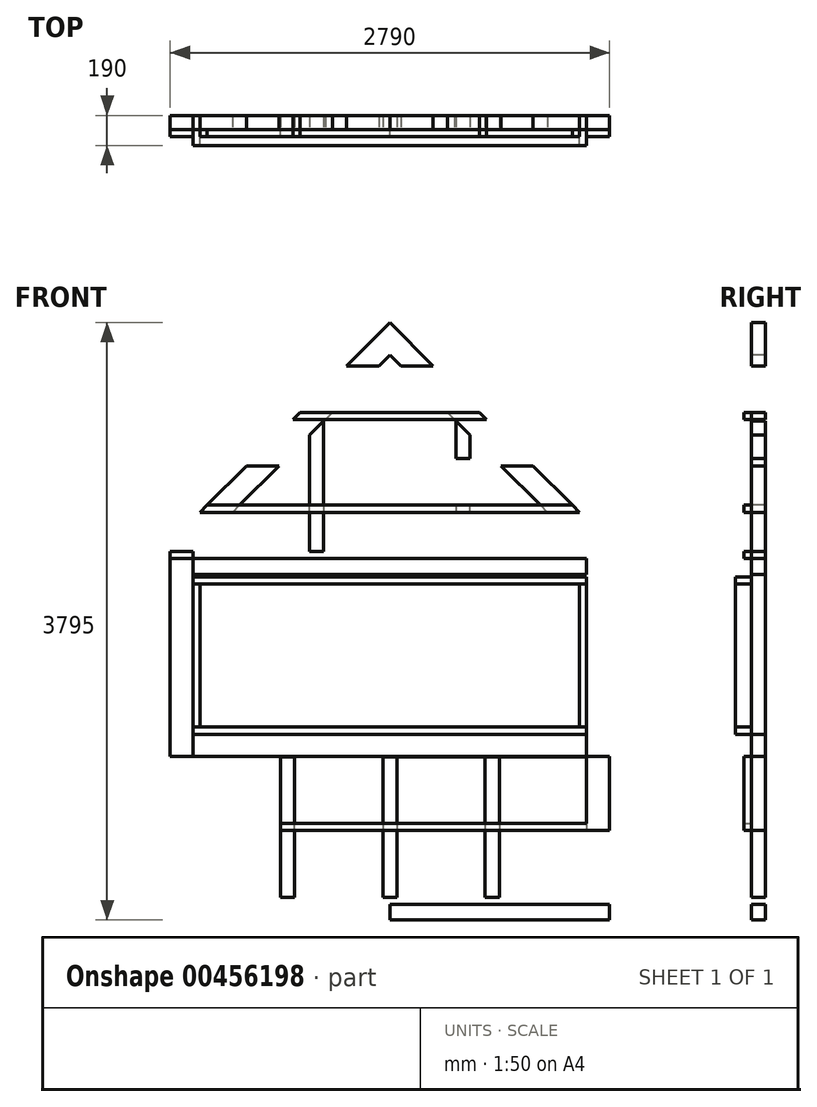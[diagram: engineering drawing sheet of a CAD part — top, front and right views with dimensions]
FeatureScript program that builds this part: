
annotation { "Feature Type Name" : "Feature", "Feature Type Description" : "" }
export const myFeature = defineFeature(function(context is Context, id is Id, definition is map)
    precondition{}
    {
        {
            var Q0;
            Q0=qCreatedBy(makeId("Front.planeOp"),FACE);
            var sketch = newSketch(context, id + "F0", { "sketchPlane" : qUnion([Q0])});
            skLineSegment(sketch, "E0.top", {"start": v(-920.12, -904.5) * mm, "end": v(-3710.12, -904.5) * mm});
            skLineSegment(sketch, "E0.left", {"start": v(-920.12, 1495.5) * mm, "end": v(-920.12, -904.5) * mm});
            skLineSegment(sketch, "E0.right", {"start": v(-3710.12, 1495.5) * mm, "end": v(-3710.12, -904.5) * mm});
            skLineSegment(sketch, "E1", {"start": v(-3710.12, 1495.5) * mm, "end": v(-2315.12, 2890.5) * mm});
            skLineSegment(sketch, "E2", {"start": v(-2315.12, 2890.5) * mm, "end": v(-920.12, 1495.5) * mm});
            skLineSegment(sketch, "E3.0", {"start": v(-2315.12, 2685.45) * mm, "end": v(-1065.12, 1435.45) * mm});
            skLineSegment(sketch, "E3.1", {"start": v(-3565.12, 1435.45) * mm, "end": v(-2315.12, 2685.45) * mm});
            skLineSegment(sketch, "E3.2", {"start": v(-1065.12, 1435.45) * mm, "end": v(-1065.12, -759.5) * mm});
            skLineSegment(sketch, "E3.3", {"start": v(-1065.12, -759.5) * mm, "end": v(-3565.12, -759.5) * mm});
            skLineSegment(sketch, "E3.4", {"start": v(-3565.12, 1435.45) * mm, "end": v(-3565.12, -759.5) * mm});
            skLineSegment(sketch, "E4.0", {"start": v(-2315.12, 2954.15) * mm, "end": v(-875.12, 1514.15) * mm});
            skLineSegment(sketch, "E4.1", {"start": v(-3755.12, 1514.15) * mm, "end": v(-2315.12, 2954.15) * mm});
            skLineSegment(sketch, "E4.2", {"start": v(-875.12, 1514.15) * mm, "end": v(-875.12, -949.5) * mm});
            skLineSegment(sketch, "E4.3", {"start": v(-875.12, -949.5) * mm, "end": v(-3755.12, -949.5) * mm});
            skLineSegment(sketch, "E4.4", {"start": v(-3755.12, 1514.15) * mm, "end": v(-3755.12, -949.5) * mm});
            skLineSegment(sketch, "E5.bottom", {"start": v(-3565.12, -759.5) * mm, "end": v(-2655.12, -759.5) * mm});
            skLineSegment(sketch, "E5.left", {"start": v(-3565.12, -759.5) * mm, "end": v(-3565.12, 1275.5) * mm});
            skLineSegment(sketch, "E6.bottom", {"start": v(-3565.12, 1435.45) * mm, "end": v(-1065.12, 1435.45) * mm});
            skLineSegment(sketch, "E6.top", {"start": v(-3565.12, 1290.45) * mm, "end": v(-1065.12, 1290.45) * mm});
            skLineSegment(sketch, "E6.left", {"start": v(-3565.12, 1435.45) * mm, "end": v(-3565.12, 1290.45) * mm});
            skLineSegment(sketch, "E6.right", {"start": v(-1065.12, 1435.45) * mm, "end": v(-1065.12, 1290.45) * mm});
            skLineSegment(sketch, "E7.left", {"start": v(-1065.12, 1275.5) * mm, "end": v(-1065.12, 275.5) * mm});
            skLineSegment(sketch, "E8.bottom", {"start": v(-3565.12, 1275.5) * mm, "end": v(-1065.12, 1275.5) * mm});
            skLineSegment(sketch, "E8.top", {"start": v(-3565.12, 275.5) * mm, "end": v(-1065.12, 275.5) * mm});
            skLineSegment(sketch, "E8.left", {"start": v(-3565.12, 1275.5) * mm, "end": v(-3565.12, 275.5) * mm});
            skLineSegment(sketch, "E9", {"start": v(-3565.12, 320.5) * mm, "end": v(-1065.12, 320.5) * mm});
            skLineSegment(sketch, "E10", {"start": v(-3565.12, 1230.5) * mm, "end": v(-1065.12, 1230.5) * mm});
            skLineSegment(sketch, "E11", {"start": v(-3520.12, 1230.5) * mm, "end": v(-3520.12, 320.5) * mm});
            skLineSegment(sketch, "E12", {"start": v(-1110.12, 1230.5) * mm, "end": v(-1110.12, 320.5) * mm});
            skLineSegment(sketch, "E13", {"start": v(-3710.12, -904.5) * mm, "end": v(-3755.12, -904.5) * mm});
            skLineSegment(sketch, "E14", {"start": v(-3455.12, -904.5) * mm, "end": v(-3555.12, -904.5) * mm});
            skLineSegment(sketch, "E15", {"start": v(-3255.12, -904.5) * mm, "end": v(-3455.12, -904.5) * mm});
            skLineSegment(sketch, "E16", {"start": v(-2315.12, 2890.5) * mm, "end": v(-2315.12, 2685.45) * mm, "construction": true});
            skLineSegment(sketch, "E17", {"start": v(-2315.12, 320.5) * mm, "end": v(-2315.12, -904.5) * mm});
            skLineSegment(sketch, "E18.bottom", {"start": v(-2315.12, 275.5) * mm, "end": v(-3565.12, 275.5) * mm});
            skLineSegment(sketch, "E18.left", {"start": v(-2315.12, 275.5) * mm, "end": v(-2315.12, 130.5) * mm});
            skLineSegment(sketch, "E18.right", {"start": v(-3565.12, 275.5) * mm, "end": v(-3565.12, 130.5) * mm});
            skLineSegment(sketch, "E19", {"start": v(-2315.12, -759.5) * mm, "end": v(-2315.12, -904.5) * mm});
            skLineSegment(sketch, "E20", {"start": v(-3565.12, 130.5) * mm, "end": v(-1065.12, 130.5) * mm});
            skLineSegment(sketch, "E21.bottom", {"start": v(-3710.12, 130.5) * mm, "end": v(-920.12, 130.5) * mm});
            skLineSegment(sketch, "E21.left", {"start": v(-3710.12, 130.5) * mm, "end": v(-3710.12, 181) * mm});
            skLineSegment(sketch, "E21.right", {"start": v(-920.12, 130.5) * mm, "end": v(-920.12, 181) * mm});
            skLineSegment(sketch, "E22.left", {"start": v(-3710.12, -305.95) * mm, "end": v(-3710.12, -350.95) * mm});
            skLineSegment(sketch, "E22.right", {"start": v(-920.12, -305.95) * mm, "end": v(-920.12, -350.95) * mm});
            skLineSegment(sketch, "E23.right", {"start": v(-920.12, -833.92) * mm, "end": v(-920.12, -788.92) * mm});
            skLineSegment(sketch, "E24.left", {"start": v(-3710.12, 1443.91) * mm, "end": v(-3710.12, 1398.91) * mm});
            skLineSegment(sketch, "E24.right", {"start": v(-920.12, 1443.91) * mm, "end": v(-920.12, 1398.91) * mm});
            skLineSegment(sketch, "E25.left", {"start": v(-3565.12, 1640.5) * mm, "end": v(-3565.12, 1585.75) * mm});
            skLineSegment(sketch, "E25.right", {"start": v(-1081.29, 1640.5) * mm, "end": v(-1081.29, 1585.75) * mm});
            skLineSegment(sketch, "E26.bottom", {"start": v(-3010.12, -759.5) * mm, "end": v(-2920.12, -759.5) * mm});
            skLineSegment(sketch, "E26.top", {"start": v(-3010.12, 130.5) * mm, "end": v(-2920.12, 130.5) * mm});
            skLineSegment(sketch, "E26.left", {"start": v(-3010.12, -759.5) * mm, "end": v(-3010.12, 130.5) * mm});
            skLineSegment(sketch, "E26.right", {"start": v(-2920.12, -759.5) * mm, "end": v(-2920.12, 130.5) * mm});
            skLineSegment(sketch, "E27.bottom", {"start": v(-1710.12, 130.5) * mm, "end": v(-1620.12, 130.5) * mm});
            skLineSegment(sketch, "E27.top", {"start": v(-1710.12, -759.5) * mm, "end": v(-1620.12, -759.5) * mm});
            skLineSegment(sketch, "E27.left", {"start": v(-1710.12, 130.5) * mm, "end": v(-1710.12, -759.5) * mm});
            skLineSegment(sketch, "E27.right", {"start": v(-1620.12, 130.5) * mm, "end": v(-1620.12, -759.5) * mm});
            skLineSegment(sketch, "E28", {"start": v(-2360.12, 130.5) * mm, "end": v(-2360.12, -759.5) * mm});
            skLineSegment(sketch, "E29.MirrorCS", {"start": v(-2270.12, 130.5) * mm, "end": v(-2270.12, -759.5) * mm});
            skLineSegment(sketch, "E30", {"start": v(-2825.12, 1435.45) * mm, "end": v(-2825.12, 2175.45) * mm});
            skLineSegment(sketch, "E31", {"start": v(-2735.12, 2265.45) * mm, "end": v(-2735.12, 1435.45) * mm});
            skLineSegment(sketch, "E32", {"start": v(-2315.12, 2685.45) * mm, "end": v(-2315.12, 130.5) * mm, "construction": true});
            skPoint(sketch, "E33", {"position": v(-2360.12, 1435.45) * mm});
            skLineSegment(sketch, "E34.MirrorCS", {"start": v(-1895.12, 2265.45) * mm, "end": v(-1895.12, 1435.45) * mm});
            skLineSegment(sketch, "E35.MirrorCS", {"start": v(-1805.12, 1435.45) * mm, "end": v(-1805.12, 2175.45) * mm});
            skLineSegment(sketch, "E36", {"start": v(-2735.12, 2265.45) * mm, "end": v(-1895.12, 2265.45) * mm});
            skLineSegment(sketch, "E37", {"start": v(-2735.12, 2175.45) * mm, "end": v(-1895.12, 2175.45) * mm});
            skLineSegment(sketch, "E38.bottom", {"start": v(-3710.12, -759.5) * mm, "end": v(-875.12, -759.5) * mm});
            skLineSegment(sketch, "E38.top", {"start": v(-3710.12, -804.5) * mm, "end": v(-875.12, -804.5) * mm});
            skLineSegment(sketch, "E38.left", {"start": v(-3710.12, -759.5) * mm, "end": v(-3710.12, -804.5) * mm});
            skLineSegment(sketch, "E38.right", {"start": v(-875.12, -759.5) * mm, "end": v(-875.12, -804.5) * mm});
            skLineSegment(sketch, "E39.bottom", {"start": v(-3710.12, -289.5) * mm, "end": v(-920.12, -289.5) * mm});
            skLineSegment(sketch, "E39.top", {"start": v(-3710.12, -334.5) * mm, "end": v(-920.12, -334.5) * mm});
            skLineSegment(sketch, "E39.left", {"start": v(-3710.12, -289.5) * mm, "end": v(-3710.12, -334.5) * mm});
            skLineSegment(sketch, "E39.right", {"start": v(-920.12, -289.5) * mm, "end": v(-920.12, -334.5) * mm});
            skLineSegment(sketch, "E40.bottom", {"start": v(-3710.12, 135.5) * mm, "end": v(-920.12, 135.5) * mm});
            skLineSegment(sketch, "E40.top", {"start": v(-3710.12, 90.5) * mm, "end": v(-920.12, 90.5) * mm});
            skLineSegment(sketch, "E40.left", {"start": v(-3710.12, 135.5) * mm, "end": v(-3710.12, 90.5) * mm});
            skLineSegment(sketch, "E40.right", {"start": v(-920.12, 135.5) * mm, "end": v(-920.12, 90.5) * mm});
            skLineSegment(sketch, "E41.bottom", {"start": v(-3710.12, 1435.45) * mm, "end": v(-920.12, 1435.45) * mm});
            skLineSegment(sketch, "E41.top", {"start": v(-3710.12, 1390.45) * mm, "end": v(-920.12, 1390.45) * mm});
            skLineSegment(sketch, "E41.left", {"start": v(-3710.12, 1435.45) * mm, "end": v(-3710.12, 1390.45) * mm});
            skLineSegment(sketch, "E41.right", {"start": v(-920.12, 1435.45) * mm, "end": v(-920.12, 1390.45) * mm});
            skLineSegment(sketch, "E42", {"start": v(-3475.18, 1730.45) * mm, "end": v(-1155.06, 1730.45) * mm});
            skLineSegment(sketch, "E43", {"start": v(-3520.18, 1685.45) * mm, "end": v(-1110.06, 1685.45) * mm});
            skLineSegment(sketch, "E44", {"start": v(-2930.18, 2275.45) * mm, "end": v(-1700.06, 2275.45) * mm});
            skLineSegment(sketch, "E45", {"start": v(-2885.18, 2320.45) * mm, "end": v(-1745.06, 2320.45) * mm});
            skLineSegment(sketch, "E46", {"start": v(-3225.18, 1980.45) * mm, "end": v(-1405.06, 1980.45) * mm});
            skLineSegment(sketch, "E47", {"start": v(-3180.18, 2025.45) * mm, "end": v(-1450.06, 2025.45) * mm});
            skLineSegment(sketch, "E48", {"start": v(-2590.18, 2615.45) * mm, "end": v(-2040.06, 2615.45) * mm});
            skLineSegment(sketch, "E49", {"start": v(-2635.18, 2570.45) * mm, "end": v(-1995.06, 2570.45) * mm});
            skSolve(sketch);
        }
        {
            var Q0;
            {var subQ0=sQuery(id+"F0.wireOp",EDGE,"E45");var subQ1=sQuery(id+"F0.wireOp",EDGE,"E3.0");var subQ2=makeQuery(id+"F0.imprint","INTERSECT",VERTEX,{"derivedFrom":[subQ1,subQ0]});Q0=makeQuery(id+"F0.imprint","IMPRINT",FACE,{"disambiguationData":[TD([[makeQuery(id+"F0.imprint","IMPRINT",EDGE,{"disambiguationData":[TD([[subQ2,-1.0]])],"derivedFrom":subQ1}),-1.0]])]});}
            var Q1;
            {var subQ0=sQuery(id+"F0.wireOp",EDGE,"E44");var subQ1=sQuery(id+"F0.wireOp",EDGE,"E1");var subQ2=makeQuery(id+"F0.imprint","INTERSECT",VERTEX,{"derivedFrom":[subQ1,subQ0]});Q1=makeQuery(id+"F0.imprint","IMPRINT",FACE,{"disambiguationData":[TD([[makeQuery(id+"F0.imprint","IMPRINT",EDGE,{"disambiguationData":[TD([[subQ2,-1.0]])],"derivedFrom":subQ1}),-1.0]])]});}
            var Q2;
            {var subQ0=sQuery(id+"F0.wireOp",EDGE,"E44");var subQ1=sQuery(id+"F0.wireOp",EDGE,"E2");var subQ2=makeQuery(id+"F0.imprint","INTERSECT",VERTEX,{"derivedFrom":[subQ1,subQ0]});Q2=makeQuery(id+"F0.imprint","IMPRINT",FACE,{"disambiguationData":[TD([[makeQuery(id+"F0.imprint","IMPRINT",EDGE,{"disambiguationData":[TD([[subQ2,1.0]])],"derivedFrom":subQ1}),-1.0]])]});}
            var Q3;
            {var subQ0=sQuery(id+"F0.wireOp",EDGE,"E42");var subQ1=sQuery(id+"F0.wireOp",EDGE,"E31");var subQ2=makeQuery(id+"F0.imprint","INTERSECT",VERTEX,{"derivedFrom":[subQ1,subQ0]});Q3=makeQuery(id+"F0.imprint","IMPRINT",FACE,{"disambiguationData":[TD([[makeQuery(id+"F0.imprint","IMPRINT",EDGE,{"disambiguationData":[TD([[subQ2,-1.0]])],"derivedFrom":subQ1}),1.0]])]});}
            var Q4;
            {var subQ0=sQuery(id+"F0.wireOp",EDGE,"E42");var subQ1=sQuery(id+"F0.wireOp",EDGE,"E34.MirrorCS");var subQ2=makeQuery(id+"F0.imprint","INTERSECT",VERTEX,{"derivedFrom":[subQ1,subQ0]});Q4=makeQuery(id+"F0.imprint","IMPRINT",FACE,{"disambiguationData":[TD([[makeQuery(id+"F0.imprint","IMPRINT",EDGE,{"disambiguationData":[TD([[subQ2,-1.0]])],"derivedFrom":subQ1}),1.0]])]});}
            var Q5;
            {var subQ0=sQuery(id+"F0.wireOp",EDGE,"E42");var subQ1=sQuery(id+"F0.wireOp",EDGE,"E3.0");var subQ2=makeQuery(id+"F0.imprint","INTERSECT",VERTEX,{"derivedFrom":[subQ1,subQ0]});Q5=makeQuery(id+"F0.imprint","IMPRINT",FACE,{"disambiguationData":[TD([[makeQuery(id+"F0.imprint","IMPRINT",EDGE,{"disambiguationData":[TD([[subQ2,-1.0]])],"derivedFrom":subQ1}),-1.0]])]});}
            var Q6;
            {var subQ0=sQuery(id+"F0.wireOp",EDGE,"E43");var subQ1=sQuery(id+"F0.wireOp",EDGE,"E3.1");var subQ2=makeQuery(id+"F0.imprint","INTERSECT",VERTEX,{"derivedFrom":[subQ1,subQ0]});Q6=makeQuery(id+"F0.imprint","IMPRINT",FACE,{"disambiguationData":[TD([[makeQuery(id+"F0.imprint","IMPRINT",EDGE,{"disambiguationData":[TD([[subQ2,-1.0]])],"derivedFrom":subQ1}),-1.0]])]});}
            var Q7;
            {var subQ0=sQuery(id+"F0.wireOp",EDGE,"E42");var subQ1=sQuery(id+"F0.wireOp",EDGE,"E1");var subQ2=makeQuery(id+"F0.imprint","INTERSECT",VERTEX,{"derivedFrom":[subQ1,subQ0]});Q7=makeQuery(id+"F0.imprint","IMPRINT",FACE,{"disambiguationData":[TD([[makeQuery(id+"F0.imprint","IMPRINT",EDGE,{"disambiguationData":[TD([[subQ2,1.0]])],"derivedFrom":subQ1}),-1.0]])]});}
            var Q8;
            {var subQ0=sQuery(id+"F0.wireOp",EDGE,"E43");var subQ1=sQuery(id+"F0.wireOp",EDGE,"E30");var subQ2=makeQuery(id+"F0.imprint","INTERSECT",VERTEX,{"derivedFrom":[subQ1,subQ0]});Q8=makeQuery(id+"F0.imprint","IMPRINT",FACE,{"disambiguationData":[TD([[makeQuery(id+"F0.imprint","IMPRINT",EDGE,{"disambiguationData":[TD([[subQ2,-1.0]])],"derivedFrom":subQ1}),-1.0]])]});}
            var Q9;
            {var subQ0=sQuery(id+"F0.wireOp",EDGE,"E41.bottom");var subQ3=makeQuery(id+"F0.imprint","INTERSECT",VERTEX,{"derivedFrom":[sQuery(id+"F0.wireOp",EDGE,"E30"),subQ0]});Q9=makeQuery(id+"F0.imprint","IMPRINT",FACE,{"disambiguationData":[TD([[makeQuery(id+"F0.imprint","IMPRINT",EDGE,{"disambiguationData":[TD([[subQ3,-1.0]])],"derivedFrom":subQ0}),-1.0]])]});}
            var Q10;
            {var subQ0=sQuery(id+"F0.wireOp",EDGE,"E41.left");var subQ7=makeQuery(id+"F0.imprint","IMPRINT",VERTEX,{"derivedFrom":subQ0});Q10=makeQuery(id+"F0.imprint","IMPRINT",FACE,{"disambiguationData":[TD([[makeQuery(id+"F0.imprint","IMPRINT",EDGE,{"disambiguationData":[TD([[subQ7,1.0]])],"derivedFrom":subQ0}),1.0]])]});}
            var Q11;
            {var subQ0=sQuery(id+"F0.wireOp",EDGE,"E41.right");var subQ8=makeQuery(id+"F0.imprint","IMPRINT",VERTEX,{"derivedFrom":subQ0});Q11=makeQuery(id+"F0.imprint","IMPRINT",FACE,{"disambiguationData":[TD([[makeQuery(id+"F0.imprint","IMPRINT",EDGE,{"disambiguationData":[TD([[subQ8,1.0]])],"derivedFrom":subQ0}),-1.0]])]});}
            var Q12;
            {var subQ0=sQuery(id+"F0.wireOp",EDGE,"E40.bottom");var subQ1=sQuery(id+"F0.wireOp",EDGE,"E3.2");var subQ2=makeQuery(id+"F0.imprint","INTERSECT",VERTEX,{"derivedFrom":[subQ1,subQ0]});Q12=makeQuery(id+"F0.imprint","IMPRINT",FACE,{"disambiguationData":[TD([[makeQuery(id+"F0.imprint","IMPRINT",EDGE,{"disambiguationData":[TD([[subQ2,-1.0]])],"derivedFrom":subQ1}),-1.0]])]});}
            var Q13;
            {var subQ0=sQuery(id+"F0.wireOp",EDGE,"E40.bottom");var subQ1=sQuery(id+"F0.wireOp",EDGE,"E18.left");var subQ2=makeQuery(id+"F0.imprint","INTERSECT",VERTEX,{"derivedFrom":[subQ1,subQ0]});Q13=makeQuery(id+"F0.imprint","IMPRINT",FACE,{"disambiguationData":[TD([[makeQuery(id+"F0.imprint","IMPRINT",EDGE,{"disambiguationData":[TD([[subQ2,-1.0]])],"derivedFrom":subQ1}),-1.0]])]});}
            var Q14;
            {var subQ5=sQuery(id+"F0.wireOp",EDGE,"E40.left");Q14=makeQuery(id+"F0.imprint","IMPRINT",FACE,{"disambiguationData":[TD([[makeQuery(id+"F0.imprint","IMPRINT",EDGE,{"derivedFrom":subQ5}),1.0]])]});}
            var Q15;
            {var subQ5=sQuery(id+"F0.wireOp",EDGE,"E40.right");Q15=makeQuery(id+"F0.imprint","IMPRINT",FACE,{"disambiguationData":[TD([[makeQuery(id+"F0.imprint","IMPRINT",EDGE,{"derivedFrom":subQ5}),-1.0]])]});}
            var Q16;
            {var subQ4=sQuery(id+"F0.wireOp",EDGE,"E39.top");var subQ6=sQuery(id+"F0.wireOp",EDGE,"E5.left");var subQ7=makeQuery(id+"F0.imprint","INTERSECT",VERTEX,{"derivedFrom":[subQ6,subQ4]});Q16=makeQuery(id+"F0.imprint","IMPRINT",FACE,{"disambiguationData":[TD([[makeQuery(id+"F0.imprint","IMPRINT",EDGE,{"disambiguationData":[TD([[subQ7,-1.0]])],"derivedFrom":subQ6}),1.0]])]});}
            var Q17;
            {var subQ0=sQuery(id+"F0.wireOp",EDGE,"E39.top");var subQ1=sQuery(id+"F0.wireOp",EDGE,"E5.left");var subQ2=makeQuery(id+"F0.imprint","INTERSECT",VERTEX,{"derivedFrom":[subQ1,subQ0]});Q17=makeQuery(id+"F0.imprint","IMPRINT",FACE,{"disambiguationData":[TD([[makeQuery(id+"F0.imprint","IMPRINT",EDGE,{"disambiguationData":[TD([[subQ2,-1.0]])],"derivedFrom":subQ1}),-1.0]])]});}
            var Q18;
            {var subQ0=sQuery(id+"F0.wireOp",EDGE,"E39.top");var subQ1=sQuery(id+"F0.wireOp",EDGE,"E26.left");var subQ2=makeQuery(id+"F0.imprint","INTERSECT",VERTEX,{"derivedFrom":[subQ1,subQ0]});Q18=makeQuery(id+"F0.imprint","IMPRINT",FACE,{"disambiguationData":[TD([[makeQuery(id+"F0.imprint","IMPRINT",EDGE,{"disambiguationData":[TD([[subQ2,-1.0]])],"derivedFrom":subQ1}),-1.0]])]});}
            var Q19;
            {var subQ0=sQuery(id+"F0.wireOp",EDGE,"E39.top");var subQ1=sQuery(id+"F0.wireOp",EDGE,"E26.right");var subQ2=makeQuery(id+"F0.imprint","INTERSECT",VERTEX,{"derivedFrom":[subQ1,subQ0]});Q19=makeQuery(id+"F0.imprint","IMPRINT",FACE,{"disambiguationData":[TD([[makeQuery(id+"F0.imprint","IMPRINT",EDGE,{"disambiguationData":[TD([[subQ2,-1.0]])],"derivedFrom":subQ1}),-1.0]])]});}
            var Q20;
            {var subQ0=sQuery(id+"F0.wireOp",EDGE,"E39.bottom");var subQ1=sQuery(id+"F0.wireOp",EDGE,"E17");var subQ2=makeQuery(id+"F0.imprint","INTERSECT",VERTEX,{"derivedFrom":[subQ1,subQ0]});Q20=makeQuery(id+"F0.imprint","IMPRINT",FACE,{"disambiguationData":[TD([[makeQuery(id+"F0.imprint","IMPRINT",EDGE,{"disambiguationData":[TD([[subQ2,-1.0]])],"derivedFrom":subQ1}),-1.0]])]});}
            var Q21;
            {var subQ0=sQuery(id+"F0.wireOp",EDGE,"E39.bottom");var subQ1=sQuery(id+"F0.wireOp",EDGE,"E17");var subQ2=makeQuery(id+"F0.imprint","INTERSECT",VERTEX,{"derivedFrom":[subQ1,subQ0]});Q21=makeQuery(id+"F0.imprint","IMPRINT",FACE,{"disambiguationData":[TD([[makeQuery(id+"F0.imprint","IMPRINT",EDGE,{"disambiguationData":[TD([[subQ2,-1.0]])],"derivedFrom":subQ1}),1.0]])]});}
            var Q22;
            {var subQ0=sQuery(id+"F0.wireOp",EDGE,"E39.bottom");var subQ1=sQuery(id+"F0.wireOp",EDGE,"E27.left");var subQ2=makeQuery(id+"F0.imprint","INTERSECT",VERTEX,{"derivedFrom":[subQ1,subQ0]});Q22=makeQuery(id+"F0.imprint","IMPRINT",FACE,{"disambiguationData":[TD([[makeQuery(id+"F0.imprint","IMPRINT",EDGE,{"disambiguationData":[TD([[subQ2,-1.0]])],"derivedFrom":subQ1}),-1.0]])]});}
            var Q23;
            {var subQ0=sQuery(id+"F0.wireOp",EDGE,"E39.bottom");var subQ1=sQuery(id+"F0.wireOp",EDGE,"E27.left");var subQ2=makeQuery(id+"F0.imprint","INTERSECT",VERTEX,{"derivedFrom":[subQ1,subQ0]});Q23=makeQuery(id+"F0.imprint","IMPRINT",FACE,{"disambiguationData":[TD([[makeQuery(id+"F0.imprint","IMPRINT",EDGE,{"disambiguationData":[TD([[subQ2,-1.0]])],"derivedFrom":subQ1}),1.0]])]});}
            var Q24;
            {var subQ0=sQuery(id+"F0.wireOp",EDGE,"E39.bottom");var subQ1=sQuery(id+"F0.wireOp",EDGE,"E3.2");var subQ2=makeQuery(id+"F0.imprint","INTERSECT",VERTEX,{"derivedFrom":[subQ1,subQ0]});Q24=makeQuery(id+"F0.imprint","IMPRINT",FACE,{"disambiguationData":[TD([[makeQuery(id+"F0.imprint","IMPRINT",EDGE,{"disambiguationData":[TD([[subQ2,-1.0]])],"derivedFrom":subQ1}),-1.0]])]});}
            var Q25;
            {var subQ1=sQuery(id+"F0.wireOp",EDGE,"E39.bottom");var subQ6=sQuery(id+"F0.wireOp",EDGE,"E3.2");var subQ8=makeQuery(id+"F0.imprint","INTERSECT",VERTEX,{"derivedFrom":[subQ6,subQ1]});Q25=makeQuery(id+"F0.imprint","IMPRINT",FACE,{"disambiguationData":[TD([[makeQuery(id+"F0.imprint","IMPRINT",EDGE,{"disambiguationData":[TD([[subQ8,-1.0]])],"derivedFrom":subQ6}),1.0]])]});}
            var Q26;
            {var subQ4=sQuery(id+"F0.wireOp",EDGE,"E38.left");Q26=makeQuery(id+"F0.imprint","IMPRINT",FACE,{"disambiguationData":[TD([[makeQuery(id+"F0.imprint","IMPRINT",EDGE,{"derivedFrom":subQ4}),1.0]])]});}
            var Q27;
            {var subQ4=sQuery(id+"F0.wireOp",EDGE,"E23.right");var subQ5=sQuery(id+"F0.wireOp",EDGE,"E0.left");var subQ6=makeQuery(id+"F0.imprint","INTERSECT",VERTEX,{"disambiguationData":[OD(1.0)],"derivedFrom":[subQ5,subQ4]});Q27=makeQuery(id+"F0.imprint","IMPRINT",FACE,{"disambiguationData":[TD([[makeQuery(id+"F0.imprint","IMPRINT",EDGE,{"disambiguationData":[TD([[subQ6,1.0]])],"derivedFrom":subQ5}),-1.0]])]});}
            var Q28;
            {var subQ0=sQuery(id+"F0.wireOp",EDGE,"E42");var subQ1=sQuery(id+"F0.wireOp",EDGE,"E2");var subQ2=makeQuery(id+"F0.imprint","INTERSECT",VERTEX,{"derivedFrom":[subQ1,subQ0]});Q28=makeQuery(id+"F0.imprint","IMPRINT",FACE,{"disambiguationData":[TD([[makeQuery(id+"F0.imprint","IMPRINT",EDGE,{"disambiguationData":[TD([[subQ2,-1.0]])],"derivedFrom":subQ1}),-1.0]])]});}
            extrude(context, id + "F1", {"entities" : qUnion([Q0, Q1, Q2, Q3, Q4, Q5, Q6, Q7, Q8, Q9, Q10, Q11, Q12, Q13, Q14, Q15, Q16, Q17, Q18, Q19, Q20, Q21, Q22, Q23, Q24, Q25, Q26, Q27, Q28]), "depth" : 45 * mm, "offsetDistance" : 25 * mm});
        }
        {
            var Q0;
            {var subQ1=sQuery(id+"F0.wireOp",EDGE,"E3.1");var subQ4=sQuery(id+"F0.wireOp",EDGE,"E30");var subQ5=makeQuery(id+"F0.imprint","INTERSECT",VERTEX,{"derivedFrom":[subQ1,subQ4]});Q0=makeQuery(id+"F0.imprint","IMPRINT",FACE,{"disambiguationData":[TD([[makeQuery(id+"F0.imprint","IMPRINT",EDGE,{"disambiguationData":[TD([[subQ5,1.0]])],"derivedFrom":subQ4}),-1.0]])]});}
            var Q1;
            {var subQ0=sQuery(id+"F0.wireOp",EDGE,"E43");var subQ1=sQuery(id+"F0.wireOp",EDGE,"E30");var subQ2=makeQuery(id+"F0.imprint","INTERSECT",VERTEX,{"derivedFrom":[subQ1,subQ0]});Q1=makeQuery(id+"F0.imprint","IMPRINT",FACE,{"disambiguationData":[TD([[makeQuery(id+"F0.imprint","IMPRINT",EDGE,{"disambiguationData":[TD([[subQ2,-1.0]])],"derivedFrom":subQ1}),-1.0]])]});}
            var Q2;
            {var subQ0=sQuery(id+"F0.wireOp",EDGE,"E41.bottom");var subQ1=sQuery(id+"F0.wireOp",EDGE,"E30");var subQ2=makeQuery(id+"F0.imprint","INTERSECT",VERTEX,{"derivedFrom":[subQ1,subQ0]});Q2=makeQuery(id+"F0.imprint","IMPRINT",FACE,{"disambiguationData":[TD([[makeQuery(id+"F0.imprint","IMPRINT",EDGE,{"disambiguationData":[TD([[subQ2,-1.0]])],"derivedFrom":subQ1}),-1.0]])]});}
            var Q3;
            {var subQ5=sQuery(id+"F0.wireOp",EDGE,"E34.MirrorCS");var subQ6=makeQuery(id+"F0.imprint","INTERSECT",VERTEX,{"derivedFrom":[subQ5,sQuery(id+"F0.wireOp",EDGE,"E37")]});Q3=makeQuery(id+"F0.imprint","IMPRINT",FACE,{"disambiguationData":[TD([[makeQuery(id+"F0.imprint","IMPRINT",EDGE,{"disambiguationData":[TD([[subQ6,-1.0]])],"derivedFrom":subQ5}),1.0]])]});}
            var Q4;
            {var subQ0=sQuery(id+"F0.wireOp",EDGE,"E42");var subQ1=sQuery(id+"F0.wireOp",EDGE,"E34.MirrorCS");var subQ2=makeQuery(id+"F0.imprint","INTERSECT",VERTEX,{"derivedFrom":[subQ1,subQ0]});Q4=makeQuery(id+"F0.imprint","IMPRINT",FACE,{"disambiguationData":[TD([[makeQuery(id+"F0.imprint","IMPRINT",EDGE,{"disambiguationData":[TD([[subQ2,-1.0]])],"derivedFrom":subQ1}),1.0]])]});}
            var Q5;
            {var subQ0=sQuery(id+"F0.wireOp",EDGE,"E41.bottom");var subQ1=sQuery(id+"F0.wireOp",EDGE,"E34.MirrorCS");var subQ2=makeQuery(id+"F0.imprint","INTERSECT",VERTEX,{"derivedFrom":[subQ1,subQ0]});Q5=makeQuery(id+"F0.imprint","IMPRINT",FACE,{"disambiguationData":[TD([[makeQuery(id+"F0.imprint","IMPRINT",EDGE,{"disambiguationData":[TD([[subQ2,1.0]])],"derivedFrom":subQ1}),1.0]])]});}
            var Q6;
            {var subQ0=sQuery(id+"F0.wireOp",EDGE,"E26.top");Q6=makeQuery(id+"F0.imprint","IMPRINT",FACE,{"disambiguationData":[TD([[makeQuery(id+"F0.imprint","IMPRINT",EDGE,{"derivedFrom":subQ0}),-1.0]])]});}
            var Q7;
            {var subQ0=sQuery(id+"F0.wireOp",EDGE,"E39.top");var subQ1=sQuery(id+"F0.wireOp",EDGE,"E26.left");var subQ2=makeQuery(id+"F0.imprint","INTERSECT",VERTEX,{"derivedFrom":[subQ1,subQ0]});Q7=makeQuery(id+"F0.imprint","IMPRINT",FACE,{"disambiguationData":[TD([[makeQuery(id+"F0.imprint","IMPRINT",EDGE,{"disambiguationData":[TD([[subQ2,-1.0]])],"derivedFrom":subQ1}),-1.0]])]});}
            var Q8;
            {var subQ0=sQuery(id+"F0.wireOp",EDGE,"E38.bottom");var subQ1=sQuery(id+"F0.wireOp",EDGE,"E26.left");var subQ2=makeQuery(id+"F0.imprint","INTERSECT",VERTEX,{"derivedFrom":[subQ1,subQ0]});Q8=makeQuery(id+"F0.imprint","IMPRINT",FACE,{"disambiguationData":[TD([[makeQuery(id+"F0.imprint","IMPRINT",EDGE,{"disambiguationData":[TD([[subQ2,-1.0]])],"derivedFrom":subQ1}),-1.0]])]});}
            var Q9;
            {var subQ0=sQuery(id+"F0.wireOp",EDGE,"E27.bottom");Q9=makeQuery(id+"F0.imprint","IMPRINT",FACE,{"disambiguationData":[TD([[makeQuery(id+"F0.imprint","IMPRINT",EDGE,{"derivedFrom":subQ0}),-1.0]])]});}
            var Q10;
            {var subQ0=sQuery(id+"F0.wireOp",EDGE,"E38.bottom");var subQ1=sQuery(id+"F0.wireOp",EDGE,"E27.left");var subQ2=makeQuery(id+"F0.imprint","INTERSECT",VERTEX,{"derivedFrom":[subQ1,subQ0]});Q10=makeQuery(id+"F0.imprint","IMPRINT",FACE,{"disambiguationData":[TD([[makeQuery(id+"F0.imprint","IMPRINT",EDGE,{"disambiguationData":[TD([[subQ2,1.0]])],"derivedFrom":subQ1}),1.0]])]});}
            var Q11;
            {var subQ0=sQuery(id+"F0.wireOp",EDGE,"E39.bottom");var subQ1=sQuery(id+"F0.wireOp",EDGE,"E27.left");var subQ2=makeQuery(id+"F0.imprint","INTERSECT",VERTEX,{"derivedFrom":[subQ1,subQ0]});Q11=makeQuery(id+"F0.imprint","IMPRINT",FACE,{"disambiguationData":[TD([[makeQuery(id+"F0.imprint","IMPRINT",EDGE,{"disambiguationData":[TD([[subQ2,-1.0]])],"derivedFrom":subQ1}),1.0]])]});}
            var Q12;
            {var subQ0=sQuery(id+"F0.wireOp",EDGE,"E21.bottom");var subQ5=sQuery(id+"F0.wireOp",EDGE,"E28");var subQ6=makeQuery(id+"F0.imprint","INTERSECT",VERTEX,{"derivedFrom":[subQ0,subQ5]});Q12=makeQuery(id+"F0.imprint","IMPRINT",FACE,{"disambiguationData":[TD([[makeQuery(id+"F0.imprint","IMPRINT",EDGE,{"disambiguationData":[TD([[subQ6,-1.0]])],"derivedFrom":subQ5}),1.0]])]});}
            var Q13;
            {var subQ0=sQuery(id+"F0.wireOp",EDGE,"E21.bottom");var subQ5=sQuery(id+"F0.wireOp",EDGE,"E29.MirrorCS");var subQ6=makeQuery(id+"F0.imprint","INTERSECT",VERTEX,{"derivedFrom":[subQ0,subQ5]});Q13=makeQuery(id+"F0.imprint","IMPRINT",FACE,{"disambiguationData":[TD([[makeQuery(id+"F0.imprint","IMPRINT",EDGE,{"disambiguationData":[TD([[subQ6,-1.0]])],"derivedFrom":subQ5}),-1.0]])]});}
            var Q14;
            {var subQ0=sQuery(id+"F0.wireOp",EDGE,"E39.bottom");var subQ1=sQuery(id+"F0.wireOp",EDGE,"E17");var subQ2=makeQuery(id+"F0.imprint","INTERSECT",VERTEX,{"derivedFrom":[subQ1,subQ0]});Q14=makeQuery(id+"F0.imprint","IMPRINT",FACE,{"disambiguationData":[TD([[makeQuery(id+"F0.imprint","IMPRINT",EDGE,{"disambiguationData":[TD([[subQ2,-1.0]])],"derivedFrom":subQ1}),-1.0]])]});}
            var Q15;
            {var subQ0=sQuery(id+"F0.wireOp",EDGE,"E39.bottom");var subQ1=sQuery(id+"F0.wireOp",EDGE,"E17");var subQ2=makeQuery(id+"F0.imprint","INTERSECT",VERTEX,{"derivedFrom":[subQ1,subQ0]});Q15=makeQuery(id+"F0.imprint","IMPRINT",FACE,{"disambiguationData":[TD([[makeQuery(id+"F0.imprint","IMPRINT",EDGE,{"disambiguationData":[TD([[subQ2,-1.0]])],"derivedFrom":subQ1}),1.0]])]});}
            var Q16;
            {var subQ0=sQuery(id+"F0.wireOp",EDGE,"E38.bottom");var subQ5=sQuery(id+"F0.wireOp",EDGE,"E28");var subQ6=makeQuery(id+"F0.imprint","INTERSECT",VERTEX,{"derivedFrom":[subQ5,subQ0]});Q16=makeQuery(id+"F0.imprint","IMPRINT",FACE,{"disambiguationData":[TD([[makeQuery(id+"F0.imprint","IMPRINT",EDGE,{"disambiguationData":[TD([[subQ6,1.0]])],"derivedFrom":subQ5}),1.0]])]});}
            var Q17;
            {var subQ0=sQuery(id+"F0.wireOp",EDGE,"E38.bottom");var subQ5=sQuery(id+"F0.wireOp",EDGE,"E29.MirrorCS");var subQ6=makeQuery(id+"F0.imprint","INTERSECT",VERTEX,{"derivedFrom":[subQ5,subQ0]});Q17=makeQuery(id+"F0.imprint","IMPRINT",FACE,{"disambiguationData":[TD([[makeQuery(id+"F0.imprint","IMPRINT",EDGE,{"disambiguationData":[TD([[subQ6,1.0]])],"derivedFrom":subQ5}),-1.0]])]});}
            extrude(context, id + "F2", {"entities" : qUnion([Q0, Q1, Q2, Q3, Q4, Q5, Q6, Q7, Q8, Q9, Q10, Q11, Q12, Q13, Q14, Q15, Q16, Q17]), "depth" : -90 * mm, "offsetDistance" : 25 * mm});
        }
        {
            var Q0;
            {var subQ5=sQuery(id+"F0.wireOp",EDGE,"E14");Q0=makeQuery(id+"F0.imprint","IMPRINT",FACE,{"disambiguationData":[TD([[makeQuery(id+"F0.imprint","IMPRINT",EDGE,{"derivedFrom":subQ5}),-1.0]])]});}
            var Q1;
            {var subQ4=sQuery(id+"F0.wireOp",EDGE,"E38.left");Q1=makeQuery(id+"F0.imprint","IMPRINT",FACE,{"disambiguationData":[TD([[makeQuery(id+"F0.imprint","IMPRINT",EDGE,{"derivedFrom":subQ4}),1.0]])]});}
            var Q2;
            {var subQ1=sQuery(id+"F0.wireOp",EDGE,"E0.top");var subQ7=sQuery(id+"F0.wireOp",EDGE,"E0.left");var subQ9=makeQuery(id+"F0.imprint","INTERSECT",VERTEX,{"derivedFrom":[subQ1,subQ7]});Q2=makeQuery(id+"F0.imprint","IMPRINT",FACE,{"disambiguationData":[TD([[makeQuery(id+"F0.imprint","IMPRINT",EDGE,{"disambiguationData":[TD([[subQ9,-1.0]])],"derivedFrom":subQ1}),-1.0]])]});}
            var Q3;
            {var subQ4=sQuery(id+"F0.wireOp",EDGE,"E23.right");var subQ5=sQuery(id+"F0.wireOp",EDGE,"E0.left");var subQ6=makeQuery(id+"F0.imprint","INTERSECT",VERTEX,{"disambiguationData":[OD(1.0)],"derivedFrom":[subQ5,subQ4]});Q3=makeQuery(id+"F0.imprint","IMPRINT",FACE,{"disambiguationData":[TD([[makeQuery(id+"F0.imprint","IMPRINT",EDGE,{"disambiguationData":[TD([[subQ6,1.0]])],"derivedFrom":subQ5}),-1.0]])]});}
            var Q4;
            {var subQ5=sQuery(id+"F0.wireOp",EDGE,"E22.right");Q4=makeQuery(id+"F0.imprint","IMPRINT",FACE,{"disambiguationData":[TD([[makeQuery(id+"F0.imprint","IMPRINT",EDGE,{"derivedFrom":subQ5}),-1.0]])]});}
            var Q5;
            {var subQ1=sQuery(id+"F0.wireOp",EDGE,"E39.bottom");var subQ6=sQuery(id+"F0.wireOp",EDGE,"E3.2");var subQ8=makeQuery(id+"F0.imprint","INTERSECT",VERTEX,{"derivedFrom":[subQ6,subQ1]});Q5=makeQuery(id+"F0.imprint","IMPRINT",FACE,{"disambiguationData":[TD([[makeQuery(id+"F0.imprint","IMPRINT",EDGE,{"disambiguationData":[TD([[subQ8,-1.0]])],"derivedFrom":subQ6}),1.0]])]});}
            var Q6;
            {var subQ0=sQuery(id+"F0.wireOp",EDGE,"E21.bottom");var subQ5=sQuery(id+"F0.wireOp",EDGE,"E3.2");var subQ6=makeQuery(id+"F0.imprint","INTERSECT",VERTEX,{"derivedFrom":[subQ5,subQ0]});Q6=makeQuery(id+"F0.imprint","IMPRINT",FACE,{"disambiguationData":[TD([[makeQuery(id+"F0.imprint","IMPRINT",EDGE,{"disambiguationData":[TD([[subQ6,-1.0]])],"derivedFrom":subQ5}),1.0]])]});}
            var Q7;
            {var subQ0=sQuery(id+"F0.wireOp",EDGE,"E21.right");Q7=makeQuery(id+"F0.imprint","IMPRINT",FACE,{"disambiguationData":[TD([[makeQuery(id+"F0.imprint","IMPRINT",EDGE,{"derivedFrom":subQ0}),1.0]])]});}
            var Q8;
            {var subQ5=sQuery(id+"F0.wireOp",EDGE,"E40.right");Q8=makeQuery(id+"F0.imprint","IMPRINT",FACE,{"disambiguationData":[TD([[makeQuery(id+"F0.imprint","IMPRINT",EDGE,{"derivedFrom":subQ5}),-1.0]])]});}
            var Q9;
            {var subQ5=sQuery(id+"F0.wireOp",EDGE,"E7.left");var subQ13=makeQuery(id+"F0.imprint","INTERSECT",VERTEX,{"derivedFrom":[subQ5,sQuery(id+"F0.wireOp",EDGE,"E9")]});Q9=makeQuery(id+"F0.imprint","IMPRINT",FACE,{"disambiguationData":[TD([[makeQuery(id+"F0.imprint","IMPRINT",EDGE,{"disambiguationData":[TD([[subQ13,1.0]])],"derivedFrom":subQ5}),1.0]])]});}
            var Q10;
            {var subQ0=sQuery(id+"F0.wireOp",EDGE,"E41.right");var subQ8=makeQuery(id+"F0.imprint","IMPRINT",VERTEX,{"derivedFrom":subQ0});Q10=makeQuery(id+"F0.imprint","IMPRINT",FACE,{"disambiguationData":[TD([[makeQuery(id+"F0.imprint","IMPRINT",EDGE,{"disambiguationData":[TD([[subQ8,1.0]])],"derivedFrom":subQ0}),-1.0]])]});}
            var Q11;
            {var subQ0=sQuery(id+"F0.wireOp",EDGE,"E24.right");Q11=makeQuery(id+"F0.imprint","IMPRINT",FACE,{"disambiguationData":[TD([[makeQuery(id+"F0.imprint","IMPRINT",EDGE,{"derivedFrom":subQ0}),-1.0]])]});}
            var Q12;
            {var subQ0=sQuery(id+"F0.wireOp",EDGE,"E42");var subQ1=sQuery(id+"F0.wireOp",EDGE,"E2");var subQ2=makeQuery(id+"F0.imprint","INTERSECT",VERTEX,{"derivedFrom":[subQ1,subQ0]});Q12=makeQuery(id+"F0.imprint","IMPRINT",FACE,{"disambiguationData":[TD([[makeQuery(id+"F0.imprint","IMPRINT",EDGE,{"disambiguationData":[TD([[subQ2,-1.0]])],"derivedFrom":subQ1}),-1.0]])]});}
            var Q13;
            {var subQ2=sQuery(id+"F0.wireOp",EDGE,"E42");var subQ7=sQuery(id+"F0.wireOp",EDGE,"E2");var subQ8=makeQuery(id+"F0.imprint","INTERSECT",VERTEX,{"derivedFrom":[subQ7,subQ2]});Q13=makeQuery(id+"F0.imprint","IMPRINT",FACE,{"disambiguationData":[TD([[makeQuery(id+"F0.imprint","IMPRINT",EDGE,{"disambiguationData":[TD([[subQ8,1.0]])],"derivedFrom":subQ7}),-1.0]])]});}
            var Q14;
            {var subQ0=sQuery(id+"F0.wireOp",EDGE,"E44");var subQ1=sQuery(id+"F0.wireOp",EDGE,"E2");var subQ2=makeQuery(id+"F0.imprint","INTERSECT",VERTEX,{"derivedFrom":[subQ1,subQ0]});Q14=makeQuery(id+"F0.imprint","IMPRINT",FACE,{"disambiguationData":[TD([[makeQuery(id+"F0.imprint","IMPRINT",EDGE,{"disambiguationData":[TD([[subQ2,1.0]])],"derivedFrom":subQ1}),-1.0]])]});}
            var Q15;
            {var subQ6=sQuery(id+"F0.wireOp",EDGE,"E2");var subQ7=sQuery(id+"F0.wireOp",EDGE,"E1");var subQ8=makeQuery(id+"F0.imprint","INTERSECT",VERTEX,{"derivedFrom":[subQ7,subQ6]});Q15=makeQuery(id+"F0.imprint","IMPRINT",FACE,{"disambiguationData":[TD([[makeQuery(id+"F0.imprint","IMPRINT",EDGE,{"disambiguationData":[TD([[subQ8,1.0]])],"derivedFrom":subQ7}),-1.0]])]});}
            var Q16;
            {var subQ0=sQuery(id+"F0.wireOp",EDGE,"E44");var subQ1=sQuery(id+"F0.wireOp",EDGE,"E1");var subQ2=makeQuery(id+"F0.imprint","INTERSECT",VERTEX,{"derivedFrom":[subQ1,subQ0]});Q16=makeQuery(id+"F0.imprint","IMPRINT",FACE,{"disambiguationData":[TD([[makeQuery(id+"F0.imprint","IMPRINT",EDGE,{"disambiguationData":[TD([[subQ2,-1.0]])],"derivedFrom":subQ1}),-1.0]])]});}
            var Q17;
            {var subQ4=sQuery(id+"F0.wireOp",EDGE,"E42");var subQ5=sQuery(id+"F0.wireOp",EDGE,"E1");var subQ6=makeQuery(id+"F0.imprint","INTERSECT",VERTEX,{"derivedFrom":[subQ5,subQ4]});Q17=makeQuery(id+"F0.imprint","IMPRINT",FACE,{"disambiguationData":[TD([[makeQuery(id+"F0.imprint","IMPRINT",EDGE,{"disambiguationData":[TD([[subQ6,-1.0]])],"derivedFrom":subQ5}),-1.0]])]});}
            var Q18;
            {var subQ0=sQuery(id+"F0.wireOp",EDGE,"E42");var subQ1=sQuery(id+"F0.wireOp",EDGE,"E1");var subQ2=makeQuery(id+"F0.imprint","INTERSECT",VERTEX,{"derivedFrom":[subQ1,subQ0]});Q18=makeQuery(id+"F0.imprint","IMPRINT",FACE,{"disambiguationData":[TD([[makeQuery(id+"F0.imprint","IMPRINT",EDGE,{"disambiguationData":[TD([[subQ2,1.0]])],"derivedFrom":subQ1}),-1.0]])]});}
            var Q19;
            {var subQ5=sQuery(id+"F0.wireOp",EDGE,"E24.left");Q19=makeQuery(id+"F0.imprint","IMPRINT",FACE,{"disambiguationData":[TD([[makeQuery(id+"F0.imprint","IMPRINT",EDGE,{"derivedFrom":subQ5}),1.0]])]});}
            var Q20;
            {var subQ0=sQuery(id+"F0.wireOp",EDGE,"E41.left");var subQ7=makeQuery(id+"F0.imprint","IMPRINT",VERTEX,{"derivedFrom":subQ0});Q20=makeQuery(id+"F0.imprint","IMPRINT",FACE,{"disambiguationData":[TD([[makeQuery(id+"F0.imprint","IMPRINT",EDGE,{"disambiguationData":[TD([[subQ7,1.0]])],"derivedFrom":subQ0}),1.0]])]});}
            var Q21;
            {var subQ0=sQuery(id+"F0.wireOp",EDGE,"E3.4");Q21=makeQuery(id+"F0.imprint","IMPRINT",FACE,{"disambiguationData":[TD([[makeQuery(id+"F0.imprint","IMPRINT",EDGE,{"derivedFrom":subQ0}),-1.0]])]});}
            var Q22;
            {var subQ5=sQuery(id+"F0.wireOp",EDGE,"E40.left");Q22=makeQuery(id+"F0.imprint","IMPRINT",FACE,{"disambiguationData":[TD([[makeQuery(id+"F0.imprint","IMPRINT",EDGE,{"derivedFrom":subQ5}),1.0]])]});}
            var Q23;
            {var subQ0=sQuery(id+"F0.wireOp",EDGE,"E21.left");Q23=makeQuery(id+"F0.imprint","IMPRINT",FACE,{"disambiguationData":[TD([[makeQuery(id+"F0.imprint","IMPRINT",EDGE,{"derivedFrom":subQ0}),-1.0]])]});}
            var Q24;
            {var subQ3=sQuery(id+"F0.wireOp",EDGE,"E39.bottom");var subQ5=sQuery(id+"F0.wireOp",EDGE,"E5.left");var subQ7=makeQuery(id+"F0.imprint","INTERSECT",VERTEX,{"derivedFrom":[subQ5,subQ3]});Q24=makeQuery(id+"F0.imprint","IMPRINT",FACE,{"disambiguationData":[TD([[makeQuery(id+"F0.imprint","IMPRINT",EDGE,{"disambiguationData":[TD([[subQ7,-1.0]])],"derivedFrom":subQ5}),1.0]])]});}
            var Q25;
            {var subQ4=sQuery(id+"F0.wireOp",EDGE,"E39.top");var subQ6=sQuery(id+"F0.wireOp",EDGE,"E5.left");var subQ7=makeQuery(id+"F0.imprint","INTERSECT",VERTEX,{"derivedFrom":[subQ6,subQ4]});Q25=makeQuery(id+"F0.imprint","IMPRINT",FACE,{"disambiguationData":[TD([[makeQuery(id+"F0.imprint","IMPRINT",EDGE,{"disambiguationData":[TD([[subQ7,-1.0]])],"derivedFrom":subQ6}),1.0]])]});}
            var Q26;
            {var subQ0=sQuery(id+"F0.wireOp",EDGE,"E22.left");Q26=makeQuery(id+"F0.imprint","IMPRINT",FACE,{"disambiguationData":[TD([[makeQuery(id+"F0.imprint","IMPRINT",EDGE,{"derivedFrom":subQ0}),1.0]])]});}
            extrude(context, id + "F3", {"entities" : qUnion([Q0, Q1, Q2, Q3, Q4, Q5, Q6, Q7, Q8, Q9, Q10, Q11, Q12, Q13, Q14, Q15, Q16, Q17, Q18, Q19, Q20, Q21, Q22, Q23, Q24, Q25, Q26]), "depth" : -90 * mm, "offsetDistance" : 25 * mm});
        }
        {
            var Q0;
            {var subQ0=sQuery(id+"F0.wireOp",EDGE,"E27.bottom");Q0=makeQuery(id+"F0.imprint","IMPRINT",FACE,{"disambiguationData":[TD([[makeQuery(id+"F0.imprint","IMPRINT",EDGE,{"derivedFrom":subQ0}),1.0]])]});}
            var Q1;
            {var subQ0=sQuery(id+"F0.wireOp",EDGE,"E40.bottom");var subQ1=sQuery(id+"F0.wireOp",EDGE,"E3.2");var subQ2=makeQuery(id+"F0.imprint","INTERSECT",VERTEX,{"derivedFrom":[subQ1,subQ0]});Q1=makeQuery(id+"F0.imprint","IMPRINT",FACE,{"disambiguationData":[TD([[makeQuery(id+"F0.imprint","IMPRINT",EDGE,{"disambiguationData":[TD([[subQ2,-1.0]])],"derivedFrom":subQ1}),-1.0]])]});}
            var Q2;
            {var subQ0=sQuery(id+"F0.wireOp",EDGE,"E8.top");Q2=makeQuery(id+"F0.imprint","IMPRINT",FACE,{"disambiguationData":[TD([[makeQuery(id+"F0.imprint","IMPRINT",EDGE,{"derivedFrom":subQ0}),-1.0]])]});}
            var Q3;
            {var subQ3=sQuery(id+"F0.wireOp",EDGE,"E26.top");Q3=makeQuery(id+"F0.imprint","IMPRINT",FACE,{"disambiguationData":[TD([[makeQuery(id+"F0.imprint","IMPRINT",EDGE,{"derivedFrom":subQ3}),1.0]])]});}
            var Q4;
            {var subQ0=sQuery(id+"F0.wireOp",EDGE,"E40.bottom");var subQ1=sQuery(id+"F0.wireOp",EDGE,"E18.left");var subQ2=makeQuery(id+"F0.imprint","INTERSECT",VERTEX,{"derivedFrom":[subQ1,subQ0]});Q4=makeQuery(id+"F0.imprint","IMPRINT",FACE,{"disambiguationData":[TD([[makeQuery(id+"F0.imprint","IMPRINT",EDGE,{"disambiguationData":[TD([[subQ2,-1.0]])],"derivedFrom":subQ1}),-1.0]])]});}
            var Q5;
            {var subQ0=sQuery(id+"F0.wireOp",EDGE,"E18.bottom");Q5=makeQuery(id+"F0.imprint","IMPRINT",FACE,{"disambiguationData":[TD([[makeQuery(id+"F0.imprint","IMPRINT",EDGE,{"derivedFrom":subQ0}),1.0]])]});}
            var Q6;
            {var subQ0=sQuery(id+"F0.wireOp",EDGE,"E6.top");Q6=makeQuery(id+"F0.imprint","IMPRINT",FACE,{"disambiguationData":[TD([[makeQuery(id+"F0.imprint","IMPRINT",EDGE,{"derivedFrom":subQ0}),1.0]])]});}
            var Q7;
            {var subQ0=sQuery(id+"F0.wireOp",EDGE,"E41.bottom");var subQ3=makeQuery(id+"F0.imprint","INTERSECT",VERTEX,{"derivedFrom":[sQuery(id+"F0.wireOp",EDGE,"E30"),subQ0]});Q7=makeQuery(id+"F0.imprint","IMPRINT",FACE,{"disambiguationData":[TD([[makeQuery(id+"F0.imprint","IMPRINT",EDGE,{"disambiguationData":[TD([[subQ3,-1.0]])],"derivedFrom":subQ0}),-1.0]])]});}
            extrude(context, id + "F4", {"entities" : qUnion([Q0, Q1, Q2, Q3, Q4, Q5, Q6, Q7]), "depth" : -90 * mm, "offsetDistance" : 25 * mm});
        }
        {
            var Q0;
            {var subQ4=sQuery(id+"F0.wireOp",EDGE,"E8.bottom");Q0=makeQuery(id+"F0.imprint","IMPRINT",FACE,{"disambiguationData":[TD([[makeQuery(id+"F0.imprint","IMPRINT",EDGE,{"derivedFrom":subQ4}),-1.0]])]});}
            var Q1;
            {var subQ0=sQuery(id+"F0.wireOp",EDGE,"E18.bottom");Q1=makeQuery(id+"F0.imprint","IMPRINT",FACE,{"disambiguationData":[TD([[makeQuery(id+"F0.imprint","IMPRINT",EDGE,{"derivedFrom":subQ0}),-1.0]])]});}
            var Q2;
            {var subQ5=sQuery(id+"F0.wireOp",EDGE,"E8.top");Q2=makeQuery(id+"F0.imprint","IMPRINT",FACE,{"disambiguationData":[TD([[makeQuery(id+"F0.imprint","IMPRINT",EDGE,{"derivedFrom":subQ5}),1.0]])]});}
            extrude(context, id + "F5", {"entities" : qUnion([Q0, Q1, Q2]), "depth" : 100 * mm, "offsetDistance" : 25 * mm});
        }
        {
            var Q0;
            {var subQ5=sQuery(id+"F0.wireOp",EDGE,"E11");Q0=makeQuery(id+"F0.imprint","IMPRINT",FACE,{"disambiguationData":[TD([[makeQuery(id+"F0.imprint","IMPRINT",EDGE,{"derivedFrom":subQ5}),-1.0]])]});}
            var Q1;
            {var subQ5=sQuery(id+"F0.wireOp",EDGE,"E12");Q1=makeQuery(id+"F0.imprint","IMPRINT",FACE,{"disambiguationData":[TD([[makeQuery(id+"F0.imprint","IMPRINT",EDGE,{"derivedFrom":subQ5}),1.0]])]});}
            extrude(context, id + "F6", {"entities" : qUnion([Q0, Q1]), "depth" : 100 * mm, "offsetDistance" : 25 * mm});
        }
    });
